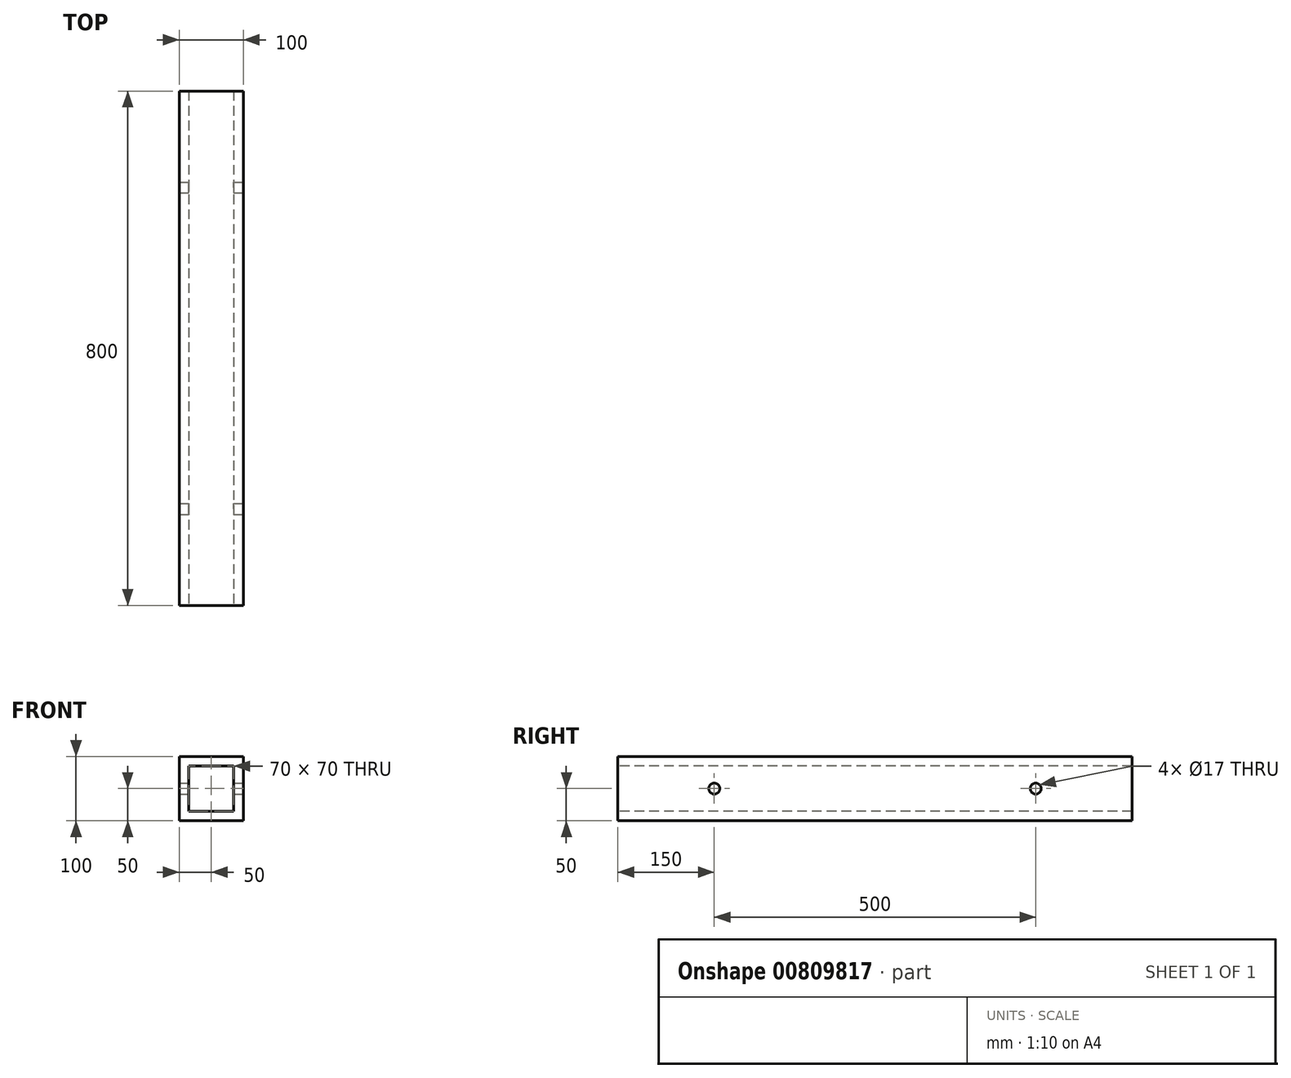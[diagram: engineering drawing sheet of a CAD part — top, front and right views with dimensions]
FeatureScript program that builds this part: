
annotation { "Feature Type Name" : "Feature", "Feature Type Description" : "" }
export const myFeature = defineFeature(function(context is Context, id is Id, definition is map)
    precondition{}
    {
        {
            var Q0;
            Q0=qCreatedBy(makeId("Front.planeOp"),FACE);
            var sketch = newSketch(context, id + "F0", { "sketchPlane" : qUnion([Q0])});
            skLineSegment(sketch, "E0.bottom", {"start": v(-50, 50) * mm, "end": v(50, 50) * mm});
            skLineSegment(sketch, "E0.top", {"start": v(-50, -50) * mm, "end": v(50, -50) * mm});
            skLineSegment(sketch, "E0.left", {"start": v(-50, 50) * mm, "end": v(-50, -50) * mm});
            skLineSegment(sketch, "E0.right", {"start": v(50, 50) * mm, "end": v(50, -50) * mm});
            skLineSegment(sketch, "E1.bottom", {"start": v(-35, 35) * mm, "end": v(35, 35) * mm});
            skLineSegment(sketch, "E1.top", {"start": v(-35, -35) * mm, "end": v(35, -35) * mm});
            skLineSegment(sketch, "E1.left", {"start": v(-35, 35) * mm, "end": v(-35, -35) * mm});
            skLineSegment(sketch, "E1.right", {"start": v(35, 35) * mm, "end": v(35, -35) * mm});
            skSolve(sketch);
        }
        {
            var Q0;
            Q0=makeQuery(id+"F0.imprint","IMPRINT",FACE,{"disambiguationData":[TD([[makeQuery(id+"F0.imprint","IMPRINT",EDGE,{"derivedFrom":sQuery(id+"F0.wireOp",EDGE,"E0.bottom")}),-1.0]])]});
            extrude(context, id + "F1", {"entities" : qUnion([Q0]), "oppositeDirection" : true, "depth" : 800 * mm, "offsetDistance" : 25 * mm});
        }
        {
            var Q0;
            Q0=makeQuery(id+"F1.opExtrude","SWEPT_FACE",FACE,{"disambiguationData":[OSD([sQuery(id+"F0.wireOp",EDGE,"E0.right")])]});
            var sketch = newSketch(context, id + "F2", { "sketchPlane" : qUnion([Q0])});
            skPoint(sketch, "E2", {"position": v(150, 0) * mm});
            skPoint(sketch, "E3", {"position": v(650, 0) * mm});
            skSolve(sketch);
        }
        {
            var Q0;
            Q0=sQuery(id+"F2.wireOp",VERTEX,"E2");
            var Q1;
            Q1=sQuery(id+"F2.wireOp",VERTEX,"E3");
            var Q2;
            Q2=makeQuery(id+"F1.opExtrude","SWEPT_BODY",BODY,{"disambiguationData":[OSD([sQuery(id+"F0.wireOp",EDGE,"E0.bottom"),sQuery(id+"F0.wireOp",EDGE,"E0.top"),sQuery(id+"F0.wireOp",EDGE,"E0.left"),sQuery(id+"F0.wireOp",EDGE,"E0.right"),sQuery(id+"F0.wireOp",EDGE,"E1.bottom"),sQuery(id+"F0.wireOp",EDGE,"E1.top"),sQuery(id+"F0.wireOp",EDGE,"E1.left"),sQuery(id+"F0.wireOp",EDGE,"E1.right")])]});
            hole(context, id + "F3", {"style" : HoleStyle.SIMPLE, "endStyle" : HoleEndStyle.THROUGH, "holeDiameter" : 17 * mm, "majorDiameter" : 5 * mm, "isTappedThrough" : true, "tappedDepth" : 12 * mm, "tapClearance" : 3, "locations" : qUnion([Q0, Q1]), "scope" : qUnion([Q2])});
        }
    });
